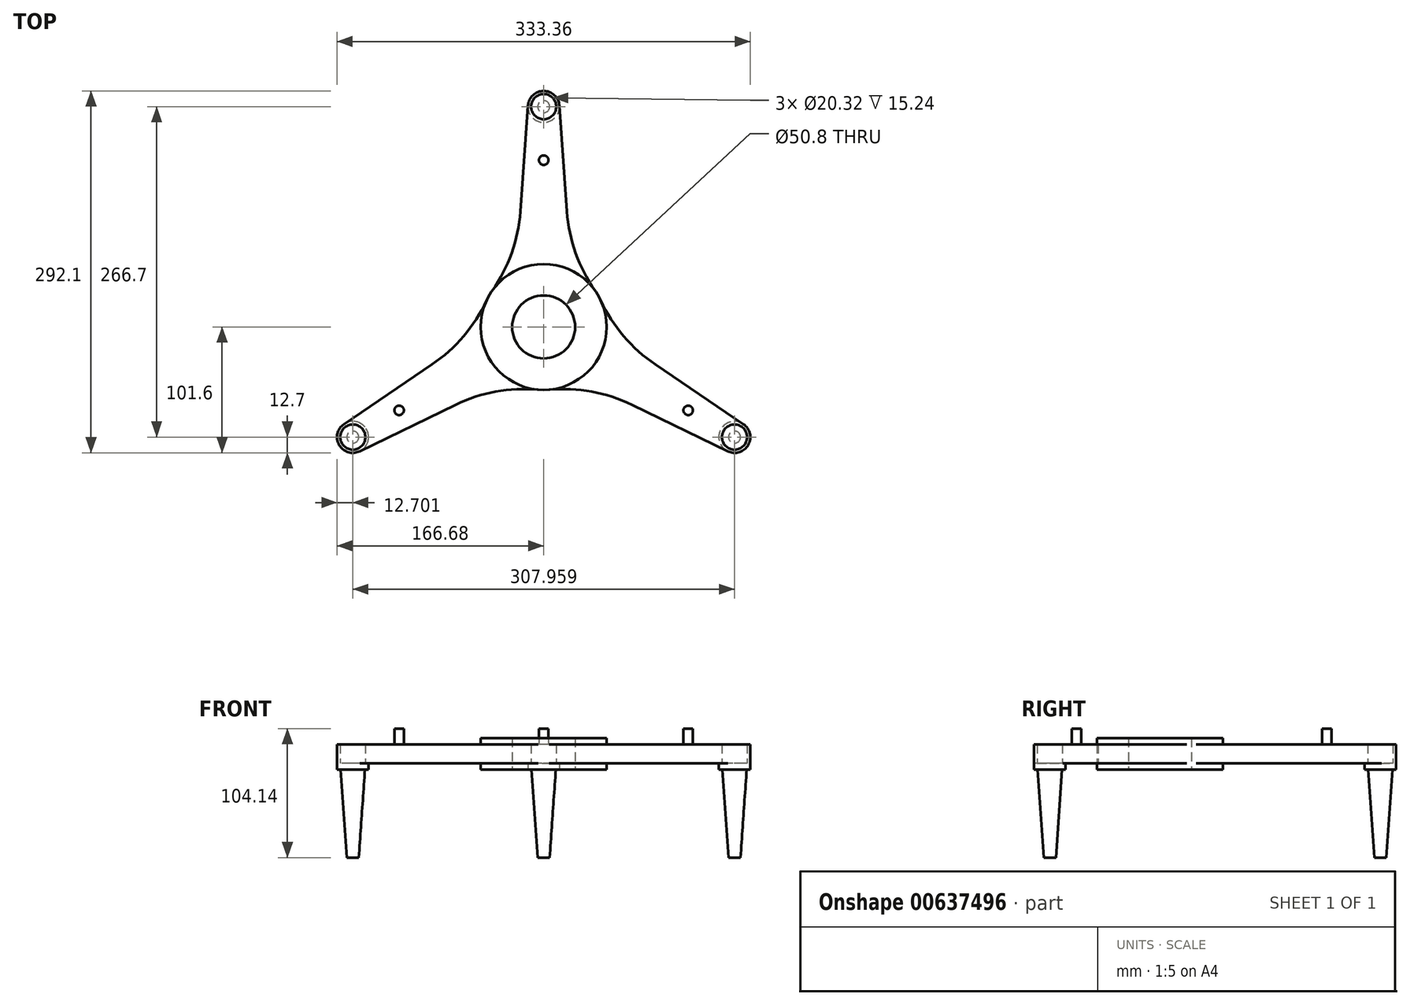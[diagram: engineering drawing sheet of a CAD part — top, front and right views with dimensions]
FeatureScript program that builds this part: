
annotation { "Feature Type Name" : "Feature", "Feature Type Description" : "" }
export const myFeature = defineFeature(function(context is Context, id is Id, definition is map)
    precondition{}
    {
        {
            var Q0;
            Q0=qCreatedBy(makeId("Top.planeOp"),FACE);
            var sketch = newSketch(context, id + "F0", { "sketchPlane" : qUnion([Q0])});
            skCircle(sketch, "E0", {"center": v(0, 0) * mm, "radius": 25.4 * mm});
            skCircle(sketch, "E1", {"center": v(0, 0) * mm, "radius": 50.8 * mm});
            skCircle(sketch, "E2", {"center": v(0, 177.8) * mm, "radius": 12.7 * mm});
            skLineSegment(sketch, "E3", {"start": v(-12.67, 178.7) * mm, "end": v(-25.34, 1.81) * mm});
            skLineSegment(sketch, "E4", {"start": v(25.34, 1.81) * mm, "end": v(12.67, 178.7) * mm});
            skArc(sketch, "E5", {"start": v(-41.56, 29.2) * mm, "mid": v(-25.83, 59.64) * mm, "end": v(-18.8, 93.16) * mm});
            skArc(sketch, "E6", {"start": v(18.8, 93.16) * mm, "mid": v(25.83, 59.64) * mm, "end": v(41.56, 29.2) * mm});
            skLineSegment(sketch, "E7.1.0", {"start": v(-148.43, -100.32) * mm, "end": v(11.1, -22.85) * mm});
            skLineSegment(sketch, "E7.1.1", {"start": v(-14.24, 21.03) * mm, "end": v(-161.1, -78.38) * mm});
            skArc(sketch, "E7.1.2", {"start": v(-4.51, -50.6) * mm, "mid": v(-38.73, -52.18) * mm, "end": v(-71.28, -62.86) * mm});
            skArc(sketch, "E7.1.3", {"start": v(-90.08, -30.3) * mm, "mid": v(-64.56, -7.45) * mm, "end": v(-46.08, 21.39) * mm});
            skCircle(sketch, "E7.1.4", {"center": v(-153.98, -88.9) * mm, "radius": 12.7 * mm});
            skLineSegment(sketch, "E7.2.0", {"start": v(161.1, -78.38) * mm, "end": v(14.24, 21.03) * mm});
            skLineSegment(sketch, "E7.2.1", {"start": v(-11.1, -22.85) * mm, "end": v(148.43, -100.32) * mm});
            skArc(sketch, "E7.2.2", {"start": v(46.08, 21.39) * mm, "mid": v(64.56, -7.45) * mm, "end": v(90.08, -30.3) * mm});
            skArc(sketch, "E7.2.3", {"start": v(71.28, -62.86) * mm, "mid": v(38.73, -52.18) * mm, "end": v(4.51, -50.6) * mm});
            skCircle(sketch, "E7.2.4", {"center": v(153.98, -88.9) * mm, "radius": 12.7 * mm});
            skCircle(sketch, "E8", {"center": v(0, 177.8) * mm, "radius": 10.16 * mm});
            skCircle(sketch, "E9.1.0", {"center": v(-153.98, -88.9) * mm, "radius": 10.16 * mm});
            skCircle(sketch, "E9.2.0", {"center": v(153.98, -88.9) * mm, "radius": 10.16 * mm});
            skSolve(sketch);
        }
        {
            var Q0;
            {var subQ0=sQuery(id+"F0.wireOp",EDGE,"E3");var subQ1=sQuery(id+"F0.wireOp",EDGE,"E0");var subQ2=makeQuery(id+"F0.imprint","INTERSECT",VERTEX,{"derivedFrom":[subQ1,subQ0]});Q0=makeQuery(id+"F0.imprint","IMPRINT",FACE,{"disambiguationData":[TD([[makeQuery(id+"F0.imprint","IMPRINT",EDGE,{"disambiguationData":[TD([[subQ2,1.0]])],"derivedFrom":subQ1}),-1.0]])]});}
            var Q1;
            {var subQ0=sQuery(id+"F0.wireOp",EDGE,"E4");var subQ1=sQuery(id+"F0.wireOp",EDGE,"E0");var subQ2=makeQuery(id+"F0.imprint","INTERSECT",VERTEX,{"derivedFrom":[subQ1,subQ0]});Q1=makeQuery(id+"F0.imprint","IMPRINT",FACE,{"disambiguationData":[TD([[makeQuery(id+"F0.imprint","IMPRINT",EDGE,{"disambiguationData":[TD([[subQ2,-1.0]])],"derivedFrom":subQ1}),-1.0]])]});}
            var Q2;
            {var subQ0=sQuery(id+"F0.wireOp",EDGE,"E7.1.0");var subQ1=sQuery(id+"F0.wireOp",EDGE,"E0");var subQ2=makeQuery(id+"F0.imprint","INTERSECT",VERTEX,{"derivedFrom":[subQ1,subQ0]});Q2=makeQuery(id+"F0.imprint","IMPRINT",FACE,{"disambiguationData":[TD([[makeQuery(id+"F0.imprint","IMPRINT",EDGE,{"disambiguationData":[TD([[subQ2,1.0]])],"derivedFrom":subQ1}),-1.0]])]});}
            var Q3;
            {var subQ1=sQuery(id+"F0.wireOp",EDGE,"E0");var subQ8=sQuery(id+"F0.wireOp",EDGE,"E4");var subQ10=makeQuery(id+"F0.imprint","INTERSECT",VERTEX,{"derivedFrom":[subQ1,subQ8]});Q3=makeQuery(id+"F0.imprint","IMPRINT",FACE,{"disambiguationData":[TD([[makeQuery(id+"F0.imprint","IMPRINT",EDGE,{"disambiguationData":[TD([[subQ10,1.0]])],"derivedFrom":subQ1}),-1.0]])]});}
            var Q4;
            {var subQ7=sQuery(id+"F0.wireOp",EDGE,"E3");var subQ8=sQuery(id+"F0.wireOp",EDGE,"E0");var subQ9=makeQuery(id+"F0.imprint","INTERSECT",VERTEX,{"derivedFrom":[subQ8,subQ7]});Q4=makeQuery(id+"F0.imprint","IMPRINT",FACE,{"disambiguationData":[TD([[makeQuery(id+"F0.imprint","IMPRINT",EDGE,{"disambiguationData":[TD([[subQ9,-1.0]])],"derivedFrom":subQ8}),-1.0]])]});}
            var Q5;
            {var subQ1=sQuery(id+"F0.wireOp",EDGE,"E1");var subQ7=makeQuery(id+"F0.imprint","INTERSECT",VERTEX,{"derivedFrom":[subQ1,sQuery(id+"F0.wireOp",EDGE,"E7.1.2")]});Q5=makeQuery(id+"F0.imprint","IMPRINT",FACE,{"disambiguationData":[TD([[makeQuery(id+"F0.imprint","IMPRINT",EDGE,{"disambiguationData":[TD([[subQ7,1.0]])],"derivedFrom":subQ1}),1.0]])]});}
            var Q6;
            {var subQ1=sQuery(id+"F0.wireOp",EDGE,"E1");var subQ7=makeQuery(id+"F0.imprint","INTERSECT",VERTEX,{"derivedFrom":[subQ1,sQuery(id+"F0.wireOp",EDGE,"E6")]});Q6=makeQuery(id+"F0.imprint","IMPRINT",FACE,{"disambiguationData":[TD([[makeQuery(id+"F0.imprint","IMPRINT",EDGE,{"disambiguationData":[TD([[subQ7,1.0]])],"derivedFrom":subQ1}),1.0]])]});}
            var Q7;
            {var subQ7=sQuery(id+"F0.wireOp",EDGE,"E7.1.1");var subQ9=sQuery(id+"F0.wireOp",EDGE,"E0");var subQ10=makeQuery(id+"F0.imprint","INTERSECT",VERTEX,{"derivedFrom":[subQ9,subQ7]});Q7=makeQuery(id+"F0.imprint","IMPRINT",FACE,{"disambiguationData":[TD([[makeQuery(id+"F0.imprint","IMPRINT",EDGE,{"disambiguationData":[TD([[subQ10,1.0]])],"derivedFrom":subQ9}),-1.0]])]});}
            var Q8;
            {var subQ1=sQuery(id+"F0.wireOp",EDGE,"E1");var subQ7=makeQuery(id+"F0.imprint","INTERSECT",VERTEX,{"derivedFrom":[subQ1,sQuery(id+"F0.wireOp",EDGE,"E5")]});Q8=makeQuery(id+"F0.imprint","IMPRINT",FACE,{"disambiguationData":[TD([[makeQuery(id+"F0.imprint","IMPRINT",EDGE,{"disambiguationData":[TD([[subQ7,1.0]])],"derivedFrom":subQ1}),1.0]])]});}
            extrude(context, id + "F1", {"entities" : qUnion([Q0, Q1, Q2, Q3, Q4, Q5, Q6, Q7, Q8]), "depth" : 20.32 * mm, "offsetDistance" : 25.4 * mm});
        }
        {
            var Q0;
            {var subQ0=sQuery(id+"F0.wireOp",EDGE,"E7.1.0");var subQ1=sQuery(id+"F0.wireOp",EDGE,"E0");var subQ2=makeQuery(id+"F0.imprint","INTERSECT",VERTEX,{"derivedFrom":[subQ1,subQ0]});Q0=makeQuery(id+"F0.imprint","IMPRINT",FACE,{"disambiguationData":[TD([[makeQuery(id+"F0.imprint","IMPRINT",EDGE,{"disambiguationData":[TD([[subQ2,1.0]])],"derivedFrom":subQ1}),-1.0]])]});}
            var Q1;
            {var subQ0=sQuery(id+"F0.wireOp",EDGE,"E4");var subQ1=sQuery(id+"F0.wireOp",EDGE,"E0");var subQ2=makeQuery(id+"F0.imprint","INTERSECT",VERTEX,{"derivedFrom":[subQ1,subQ0]});Q1=makeQuery(id+"F0.imprint","IMPRINT",FACE,{"disambiguationData":[TD([[makeQuery(id+"F0.imprint","IMPRINT",EDGE,{"disambiguationData":[TD([[subQ2,-1.0]])],"derivedFrom":subQ1}),-1.0]])]});}
            var Q2;
            {var subQ0=sQuery(id+"F0.wireOp",EDGE,"E3");var subQ1=sQuery(id+"F0.wireOp",EDGE,"E0");var subQ2=makeQuery(id+"F0.imprint","INTERSECT",VERTEX,{"derivedFrom":[subQ1,subQ0]});Q2=makeQuery(id+"F0.imprint","IMPRINT",FACE,{"disambiguationData":[TD([[makeQuery(id+"F0.imprint","IMPRINT",EDGE,{"disambiguationData":[TD([[subQ2,1.0]])],"derivedFrom":subQ1}),-1.0]])]});}
            var Q3;
            {var subQ7=sQuery(id+"F0.wireOp",EDGE,"E3");var subQ8=sQuery(id+"F0.wireOp",EDGE,"E0");var subQ9=makeQuery(id+"F0.imprint","INTERSECT",VERTEX,{"derivedFrom":[subQ8,subQ7]});Q3=makeQuery(id+"F0.imprint","IMPRINT",FACE,{"disambiguationData":[TD([[makeQuery(id+"F0.imprint","IMPRINT",EDGE,{"disambiguationData":[TD([[subQ9,-1.0]])],"derivedFrom":subQ8}),-1.0]])]});}
            var Q4;
            {var subQ1=sQuery(id+"F0.wireOp",EDGE,"E1");var subQ7=makeQuery(id+"F0.imprint","INTERSECT",VERTEX,{"derivedFrom":[subQ1,sQuery(id+"F0.wireOp",EDGE,"E7.1.2")]});Q4=makeQuery(id+"F0.imprint","IMPRINT",FACE,{"disambiguationData":[TD([[makeQuery(id+"F0.imprint","IMPRINT",EDGE,{"disambiguationData":[TD([[subQ7,1.0]])],"derivedFrom":subQ1}),1.0]])]});}
            var Q5;
            {var subQ1=sQuery(id+"F0.wireOp",EDGE,"E0");var subQ8=sQuery(id+"F0.wireOp",EDGE,"E4");var subQ10=makeQuery(id+"F0.imprint","INTERSECT",VERTEX,{"derivedFrom":[subQ1,subQ8]});Q5=makeQuery(id+"F0.imprint","IMPRINT",FACE,{"disambiguationData":[TD([[makeQuery(id+"F0.imprint","IMPRINT",EDGE,{"disambiguationData":[TD([[subQ10,1.0]])],"derivedFrom":subQ1}),-1.0]])]});}
            var Q6;
            {var subQ1=sQuery(id+"F0.wireOp",EDGE,"E1");var subQ7=makeQuery(id+"F0.imprint","INTERSECT",VERTEX,{"derivedFrom":[subQ1,sQuery(id+"F0.wireOp",EDGE,"E6")]});Q6=makeQuery(id+"F0.imprint","IMPRINT",FACE,{"disambiguationData":[TD([[makeQuery(id+"F0.imprint","IMPRINT",EDGE,{"disambiguationData":[TD([[subQ7,1.0]])],"derivedFrom":subQ1}),1.0]])]});}
            var Q7;
            {var subQ7=sQuery(id+"F0.wireOp",EDGE,"E7.1.1");var subQ9=sQuery(id+"F0.wireOp",EDGE,"E0");var subQ10=makeQuery(id+"F0.imprint","INTERSECT",VERTEX,{"derivedFrom":[subQ9,subQ7]});Q7=makeQuery(id+"F0.imprint","IMPRINT",FACE,{"disambiguationData":[TD([[makeQuery(id+"F0.imprint","IMPRINT",EDGE,{"disambiguationData":[TD([[subQ10,1.0]])],"derivedFrom":subQ9}),-1.0]])]});}
            var Q8;
            {var subQ1=sQuery(id+"F0.wireOp",EDGE,"E1");var subQ7=makeQuery(id+"F0.imprint","INTERSECT",VERTEX,{"derivedFrom":[subQ1,sQuery(id+"F0.wireOp",EDGE,"E5")]});Q8=makeQuery(id+"F0.imprint","IMPRINT",FACE,{"disambiguationData":[TD([[makeQuery(id+"F0.imprint","IMPRINT",EDGE,{"disambiguationData":[TD([[subQ7,1.0]])],"derivedFrom":subQ1}),1.0]])]});}
            extrude(context, id + "F2", {"entities" : qUnion([Q0, Q1, Q2, Q3, Q4, Q5, Q6, Q7, Q8]), "operationType" : NewBodyOperationType.ADD, "oppositeDirection" : true, "depth" : 5.08 * mm, "offsetDistance" : 25.4 * mm});
        }
        {
            var Q0;
            Q0 = qSketchRegion(id + "F0", true);
            extrude(context, id + "F3", {"entities" : qUnion([Q0]), "operationType" : NewBodyOperationType.ADD, "depth" : 15.24 * mm, "offsetDistance" : 25.4 * mm});
        }
        {
            var Q0;
            Q0=makeQuery(id+"F0.imprint","IMPRINT",FACE,{"disambiguationData":[TD([[makeQuery(id+"F0.imprint","IMPRINT",EDGE,{"derivedFrom":sQuery(id+"F0.wireOp",EDGE,"E9.2.0")}),-1.0]])]});
            var Q1;
            Q1=makeQuery(id+"F0.imprint","IMPRINT",FACE,{"disambiguationData":[TD([[makeQuery(id+"F0.imprint","IMPRINT",EDGE,{"derivedFrom":sQuery(id+"F0.wireOp",EDGE,"E9.2.0")}),1.0]])]});
            var Q2;
            Q2=makeQuery(id+"F0.imprint","IMPRINT",FACE,{"disambiguationData":[TD([[makeQuery(id+"F0.imprint","IMPRINT",EDGE,{"derivedFrom":sQuery(id+"F0.wireOp",EDGE,"E9.1.0")}),1.0]])]});
            var Q3;
            Q3=makeQuery(id+"F0.imprint","IMPRINT",FACE,{"disambiguationData":[TD([[makeQuery(id+"F0.imprint","IMPRINT",EDGE,{"derivedFrom":sQuery(id+"F0.wireOp",EDGE,"E9.1.0")}),-1.0]])]});
            var Q4;
            Q4=makeQuery(id+"F0.imprint","IMPRINT",FACE,{"disambiguationData":[TD([[makeQuery(id+"F0.imprint","IMPRINT",EDGE,{"derivedFrom":sQuery(id+"F0.wireOp",EDGE,"E8")}),-1.0]])]});
            var Q5;
            Q5=makeQuery(id+"F0.imprint","IMPRINT",FACE,{"disambiguationData":[TD([[makeQuery(id+"F0.imprint","IMPRINT",EDGE,{"derivedFrom":sQuery(id+"F0.wireOp",EDGE,"E8")}),1.0]])]});
            extrude(context, id + "F4", {"entities" : qUnion([Q0, Q1, Q2, Q3, Q4, Q5]), "operationType" : NewBodyOperationType.ADD, "oppositeDirection" : true, "depth" : 5.08 * mm, "offsetDistance" : 25.4 * mm});
        }
        {
            var Q0;
            Q0=makeQuery(id+"F0.imprint","IMPRINT",FACE,{"disambiguationData":[TD([[makeQuery(id+"F0.imprint","IMPRINT",EDGE,{"derivedFrom":sQuery(id+"F0.wireOp",EDGE,"E8")}),1.0]])]});
            var Q1;
            Q1=makeQuery(id+"F0.imprint","IMPRINT",FACE,{"disambiguationData":[TD([[makeQuery(id+"F0.imprint","IMPRINT",EDGE,{"derivedFrom":sQuery(id+"F0.wireOp",EDGE,"E9.2.0")}),1.0]])]});
            var Q2;
            Q2=makeQuery(id+"F0.imprint","IMPRINT",FACE,{"disambiguationData":[TD([[makeQuery(id+"F0.imprint","IMPRINT",EDGE,{"derivedFrom":sQuery(id+"F0.wireOp",EDGE,"E9.1.0")}),1.0]])]});
            extrude(context, id + "F5", {"entities" : qUnion([Q0, Q1, Q2]), "operationType" : NewBodyOperationType.ADD, "oppositeDirection" : true, "depth" : 76.2 * mm, "offsetDistance" : 25.4 * mm, "hasDraft" : true, "draftAngle" : 4 * degree, "draftPullDirection" : true});
        }
        {
            var Q0;
            {var subQ0=sQuery(id+"F0.wireOp",EDGE,"E7.2.4");var subQ1=sQuery(id+"F0.wireOp",EDGE,"E7.2.0");var subQ2=sQuery(id+"F0.wireOp",EDGE,"E7.2.2");var subQ3=sQuery(id+"F0.wireOp",EDGE,"E1");var subQ4=sQuery(id+"F0.wireOp",EDGE,"E7.2.1");var subQ5=sQuery(id+"F0.wireOp",EDGE,"E7.2.3");var subQ6=sQuery(id+"F0.wireOp",EDGE,"E9.2.0");Q0=makeQuery(id+"F3.boolean.opBoolean","SPLIT",FACE,{"disambiguationData":[TD([makeQuery(id+"F3.opExtrude","SWEPT_FACE",FACE,{"disambiguationData":[OSD([subQ2])]})])],"derivedFrom":makeQuery(id+"F3.opExtrude","CAP_FACE",FACE,{"disambiguationData":[OSD([subQ3,sQuery(id+"F0.wireOp",EDGE,"E2"),sQuery(id+"F0.wireOp",EDGE,"E3"),sQuery(id+"F0.wireOp",EDGE,"E4"),sQuery(id+"F0.wireOp",EDGE,"E5"),sQuery(id+"F0.wireOp",EDGE,"E6"),sQuery(id+"F0.wireOp",EDGE,"E7.1.0"),sQuery(id+"F0.wireOp",EDGE,"E7.1.1"),sQuery(id+"F0.wireOp",EDGE,"E7.1.2"),sQuery(id+"F0.wireOp",EDGE,"E7.1.3"),sQuery(id+"F0.wireOp",EDGE,"E7.1.4"),subQ1,subQ4,subQ2,subQ5,subQ0,sQuery(id+"F0.wireOp",EDGE,"E8"),sQuery(id+"F0.wireOp",EDGE,"E9.1.0"),subQ6])],"isStart":false})});}
            var sketch = newSketch(context, id + "F6", { "sketchPlane" : qUnion([Q0])});
            skCircle(sketch, "E10", {"center": v(116.58, -67.31) * mm, "radius": 3.81 * mm});
            skPoint(sketch, "E11.center", {"position": v(0, 0) * mm});
            skCircle(sketch, "E12.1.0", {"center": v(0, 134.62) * mm, "radius": 3.81 * mm});
            skCircle(sketch, "E12.2.0", {"center": v(-116.59, -67.3) * mm, "radius": 3.81 * mm});
            skSolve(sketch);
        }
        {
            var Q0;
            Q0 = qSketchRegion(id + "F6", true);
            extrude(context, id + "F7", {"entities" : qUnion([Q0]), "operationType" : NewBodyOperationType.ADD, "depth" : 12.7 * mm, "offsetDistance" : 25.4 * mm});
        }
    });
